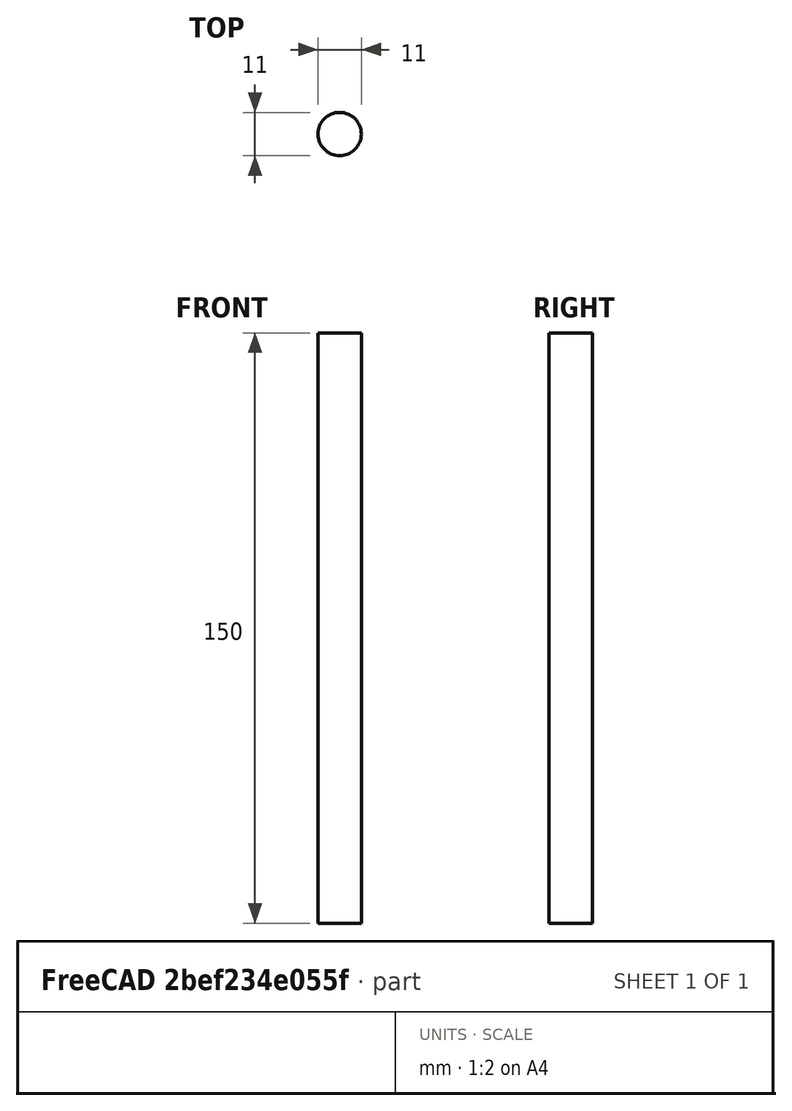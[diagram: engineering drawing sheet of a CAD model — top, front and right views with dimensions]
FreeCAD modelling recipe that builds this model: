
FCSTD DOCUMENT  (FreeCAD 2023.521R14555 (Git shallow))
Label: Interconnect_shaft
License: All rights reserved
LicenseURL: http://en.wikipedia.org/wiki/All_rights_reserved
objects: PartDesign::CoordinateSystem×2, Sketcher::SketchObject×1, PartDesign::Pad×1, PartDesign::Body×1, App::FeaturePython×1, App::Part×1
note: 8 computed .brp shape members not serialized (recipe doc carries the construction recipe); baked Part::Feature solids carry a one-line shape summary decoded from their .brp

FEATURE [Sketcher::SketchObject] Sketch
  ArcFitTolerance = 0
  AttachmentSupport = -> [XY_Plane001]
  ExternalBSplineMaxDegree = 0
  ExternalBSplineTolerance = 0
  FullyConstrained = true
  InternalTolerance = 1e-06
  InvalidShape = false
  MakeInternals = false
  MapMode = 5
  Support = -> [XY_Plane001]
  TreeRank = 0
  ValidateShape = false
  sketch-geometry (1):
    g0: Circle CenterX=0 CenterY=0 CenterZ=0 NormalX=0 NormalY=0 NormalZ=1 AngleXU=0 Radius=5.5
  constraints (2):
    c: Coincident(g0,g-1)
    c: Diameter(g0) = 11
FEATURE [PartDesign::Pad] Pad
  AddSubType = 0
  AutoTaperInnerAngle = true
  CheckUpToFaceLimits = true
  ClaimChildren = false
  Direction = (0,0,1)
  Fit = 0
  FitJoin = 0
  InnerFit = 0
  InnerFitJoin = 0
  InvalidShape = false
  Length = 150
  Length2 = 10
  NewSolid = false
  Profile = -> Sketch
  ReferenceAxis = -> Sketch [N_Axis]
  Suppress = false
  TaperInnerAngle = 0
  TaperInnerAngleRev = 0
  TreeRank = 0
  Type = 0
  ValidateShape = true
  _ProfileBasedVersion = 0
  expr: Length = Variables.Con_Len
FEATURE [PartDesign::Body] Body
  AutoGroupSolids = false
  ClaimAllChildren = false
  ExportMode = 0
  Group = -> [Sketch,Pad]
  InvalidShape = false
  Origin = -> Origin001
  Tip = -> Pad
  TreeRank = 0
  ValidateShape = false
  _ExportChildren = -> [Pad]
  _GroupVersion = 1
FEATURE [App::FeaturePython] Variables  # WARN: FeaturePython — macro-defined, semantics opaque (R4)
  Con_Len = 150
  TreeRank = 0
  Type = App::PropertyContainer
FEATURE [PartDesign::CoordinateSystem] Local_CS  label="Start"
  AttacherType = Attacher::AttachEngine3D
  AttachmentSupport = -> [Pad]
  InvalidShape = false
  MapMode = 11
  Placement = pos=(0,0,0) rot=(0,0,1;1.5708rad)
  Support = -> [Pad]
  TreeRank = 1
  ValidateShape = false
FEATURE [PartDesign::CoordinateSystem] Local_CS001  label="End"
  AttacherType = Attacher::AttachEngine3D
  AttachmentSupport = -> [Pad]
  InvalidShape = false
  MapMode = 11
  Placement = pos=(0,0,150) rot=(0,0,1;1.5708rad)
  Support = -> [Pad]
  TreeRank = 2
  ValidateShape = false
FEATURE [App::Part] Icon_Shaft
  ClaimAllChildren = false
  ExportMode = 1
  Group = -> [Body,Local_CS,Local_CS001]
  Origin = -> Origin
  TreeRank = 0
  _ExportChildren = -> [Body,Local_CS,Local_CS001]
  _GroupVersion = 1
